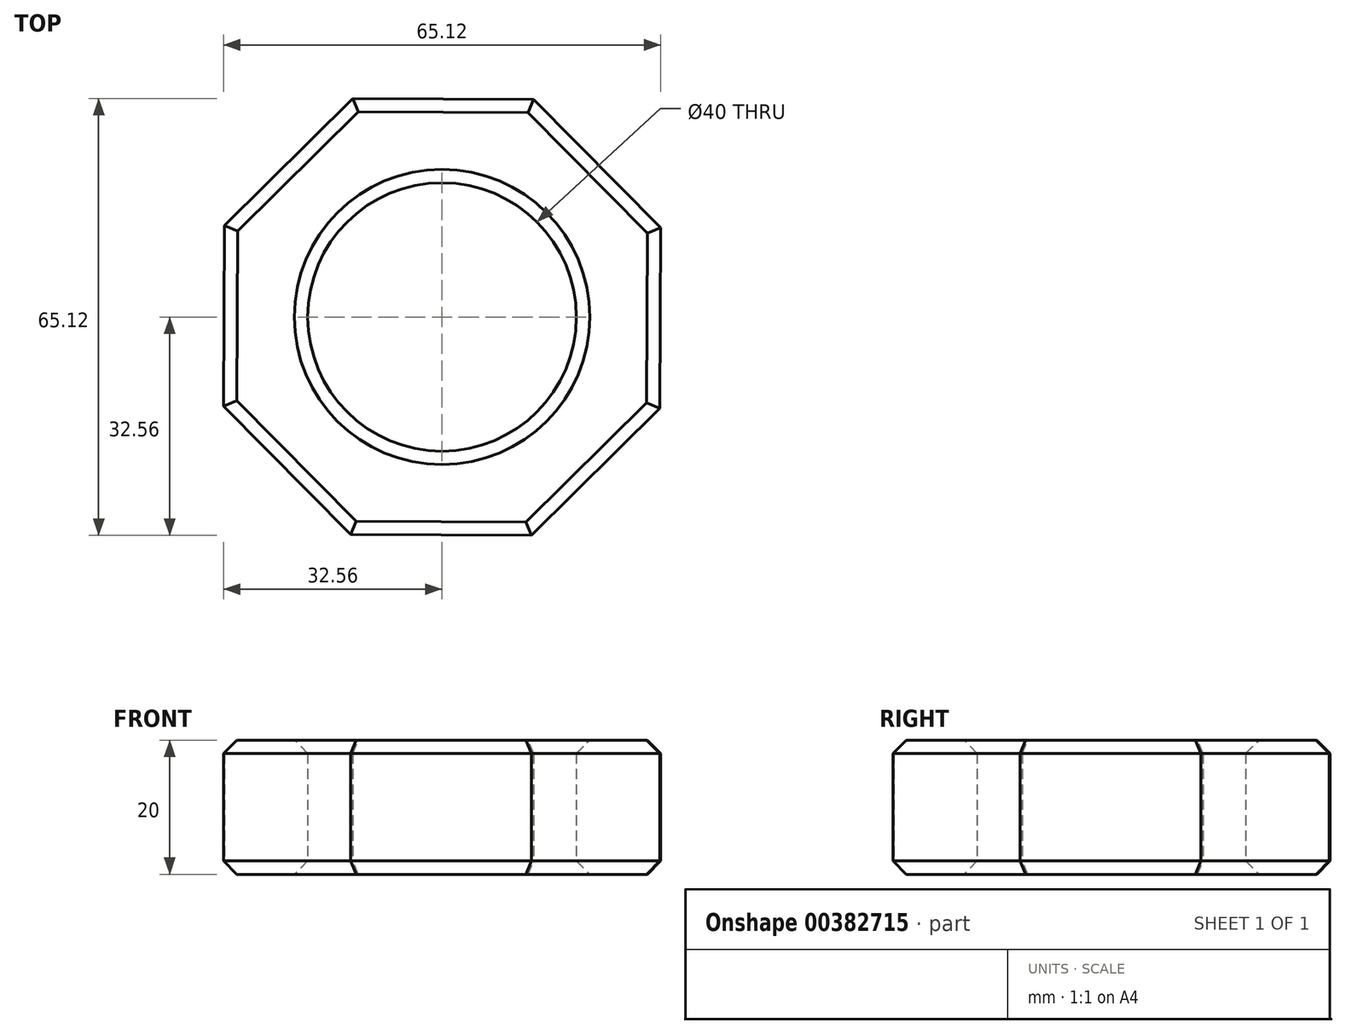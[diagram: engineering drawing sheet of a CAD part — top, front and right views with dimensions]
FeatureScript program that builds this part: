
annotation { "Feature Type Name" : "Feature", "Feature Type Description" : "" }
export const myFeature = defineFeature(function(context is Context, id is Id, definition is map)
    precondition{}
    {
        {
            var Q0;
            Q0=qCreatedBy(makeId("Top.planeOp"),FACE);
            var sketch = newSketch(context, id + "F0", { "sketchPlane" : qUnion([Q0])});
            skCircle(sketch, "E0.cCircle", {"center": v(0, 0) * mm, "radius": 32.5 * mm, "construction": true});
            skLineSegment(sketch, "E0.0", {"start": v(13.62, 32.44) * mm, "end": v(32.56, 13.3) * mm});
            skLineSegment(sketch, "E0.1", {"start": v(32.56, 13.3) * mm, "end": v(32.44, -13.62) * mm});
            skLineSegment(sketch, "E0.2", {"start": v(32.44, -13.62) * mm, "end": v(13.3, -32.56) * mm});
            skLineSegment(sketch, "E0.3", {"start": v(13.3, -32.56) * mm, "end": v(-13.62, -32.44) * mm});
            skLineSegment(sketch, "E0.4", {"start": v(-13.62, -32.44) * mm, "end": v(-32.56, -13.3) * mm});
            skLineSegment(sketch, "E0.5", {"start": v(-32.56, -13.3) * mm, "end": v(-32.44, 13.62) * mm});
            skLineSegment(sketch, "E0.6", {"start": v(-32.44, 13.62) * mm, "end": v(-13.3, 32.56) * mm});
            skLineSegment(sketch, "E0.7", {"start": v(-13.3, 32.56) * mm, "end": v(13.62, 32.44) * mm});
            skPoint(sketch, "E0.0.midPoint", {"position": v(23.1, 22.87) * mm});
            skSolve(sketch);
        }
        {
            var Q0;
            Q0 = qSketchRegion(id + "F0", true);
            extrude(context, id + "F1", {"entities" : qUnion([Q0]), "depth" : 20 * mm});
        }
        {
            var Q0;
            Q0=makeQuery(id+"F1.opExtrude","CAP_FACE",FACE,{"disambiguationData":[OSD([sQuery(id+"F0.wireOp",EDGE,"E0.0"),sQuery(id+"F0.wireOp",EDGE,"E0.1"),sQuery(id+"F0.wireOp",EDGE,"E0.2"),sQuery(id+"F0.wireOp",EDGE,"E0.3"),sQuery(id+"F0.wireOp",EDGE,"E0.4"),sQuery(id+"F0.wireOp",EDGE,"E0.5"),sQuery(id+"F0.wireOp",EDGE,"E0.6"),sQuery(id+"F0.wireOp",EDGE,"E0.7")])],"isStart":true});
            var sketch = newSketch(context, id + "F2", { "sketchPlane" : qUnion([Q0])});
            skCircle(sketch, "E1", {"center": v(0, 0) * mm, "radius": 20 * mm});
            skSolve(sketch);
        }
        {
            var Q0;
            Q0 = qSketchRegion(id + "F2", true);
            extrude(context, id + "F3", {"entities" : qUnion([Q0]), "operationType" : NewBodyOperationType.REMOVE, "endBound" : BoundingType.THROUGH_ALL, "oppositeDirection" : true, "depth" : 25 * mm});
        }
        {
            var Q0;
            Q0=makeQuery(id+"F1.opExtrude","CAP_FACE",FACE,{"disambiguationData":[OSD([sQuery(id+"F0.wireOp",EDGE,"E0.0"),sQuery(id+"F0.wireOp",EDGE,"E0.1"),sQuery(id+"F0.wireOp",EDGE,"E0.2"),sQuery(id+"F0.wireOp",EDGE,"E0.3"),sQuery(id+"F0.wireOp",EDGE,"E0.4"),sQuery(id+"F0.wireOp",EDGE,"E0.5"),sQuery(id+"F0.wireOp",EDGE,"E0.6"),sQuery(id+"F0.wireOp",EDGE,"E0.7")])],"isStart":false});
            var Q1;
            Q1=makeQuery(id+"F1.opExtrude","CAP_FACE",FACE,{"disambiguationData":[OSD([sQuery(id+"F0.wireOp",EDGE,"E0.0"),sQuery(id+"F0.wireOp",EDGE,"E0.1"),sQuery(id+"F0.wireOp",EDGE,"E0.2"),sQuery(id+"F0.wireOp",EDGE,"E0.3"),sQuery(id+"F0.wireOp",EDGE,"E0.4"),sQuery(id+"F0.wireOp",EDGE,"E0.5"),sQuery(id+"F0.wireOp",EDGE,"E0.6"),sQuery(id+"F0.wireOp",EDGE,"E0.7")])],"isStart":true});
            chamfer(context, id + "F4", {"entities" : qUnion([Q0, Q1]), "width" : 2 * mm, "tangentPropagation" : true});
        }
    });
